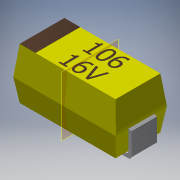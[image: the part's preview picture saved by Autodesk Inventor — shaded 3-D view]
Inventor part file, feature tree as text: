
AUTODESK INVENTOR PART (.ipt)
format: ipt  version: 2018 (Build 220112000, 112)  size: 372,736 bytes
history: native  units: mm
features: chamfer x8, extrude x5, sketch x5, fillet x2, plane x1, mirror x1, projected_geometry x1
ambient origin geometry x8: Origin, YZ Plane, XZ Plane, XY Plane, X Axis, Y Axis, Z Axis, Center Point
bodies: Solid1 (feature_tree)
feature tree (23):
  extrude  "Extrusion1"  Depth=3.2mm
  chamfer  "Chamfer2"  Distance=1.6mm
  chamfer  "Chamfer3"  Distance=0.9mm Angle=45.0deg
  chamfer  "Chamfer4"  Distance=0.9mm Angle=45.0deg
  chamfer  "Chamfer5"  Distance=0.9mm Angle=45.0deg
  chamfer  "Chamfer6"  Distance=0.7mm Angle=45.0deg
  chamfer  "Chamfer7"  Distance=0.7mm Angle=45.0deg
  chamfer  "Chamfer8"  Distance=0.7mm Angle=45.0deg
  extrude  "Extrusion2"  Depth=0.8mm
  extrude  "Extrusion3"  Depth=0.1mm
  plane  "Work Plane1"
  mirror  "Mirror1"
  fillet  "Fillet1"  Radius=0.1mm
  fillet  "Fillet2"  Radius=0.1mm
  chamfer  "Chamfer9"  Distance=0.8mm
  extrude  "Extrusion4"  Depth=0.05mm
  extrude  "Extrusion5"  Depth=0.8mm TaperAngle=45.0deg
  sketch  "Sketch1"  dims[d0=1.6mm d1=3.2mm d2=1.6mm d3=0.0mm d7=0.9mm d8=0.1mm d9=45.0deg d10=0.9mm d11=0.1mm d12=45.0deg d13=0.9mm d14=0.1mm d15=45.0deg d16=0.7mm d17=0.1mm d18=45.0deg d19=0.7mm d20=0.1mm d21=45.0deg d22=0.7mm d23=0.1mm d24=45.0deg]
  sketch  "Sketch2"  dims[d25=0.7mm d26=0.1mm d27=45.0deg d28=0.8mm]
  projected_geometry  "Projected Loop1"
  sketch  "Sketch3"  dims[d29=0.4mm d30=0.1mm d31=0.1mm d32=0.0mm d33=0.1mm d34=0.8mm d35=0.0mm]
  sketch  "Sketch4"  dims[d36=1.6mm d37=0.05mm]
  sketch  "Sketch5"  dims[d38=0.1mm d39=0.8mm d40=0.1mm d41=45.0deg d42=0.001mm d43=0.0mm d44=0.001mm d45=0.0mm]
